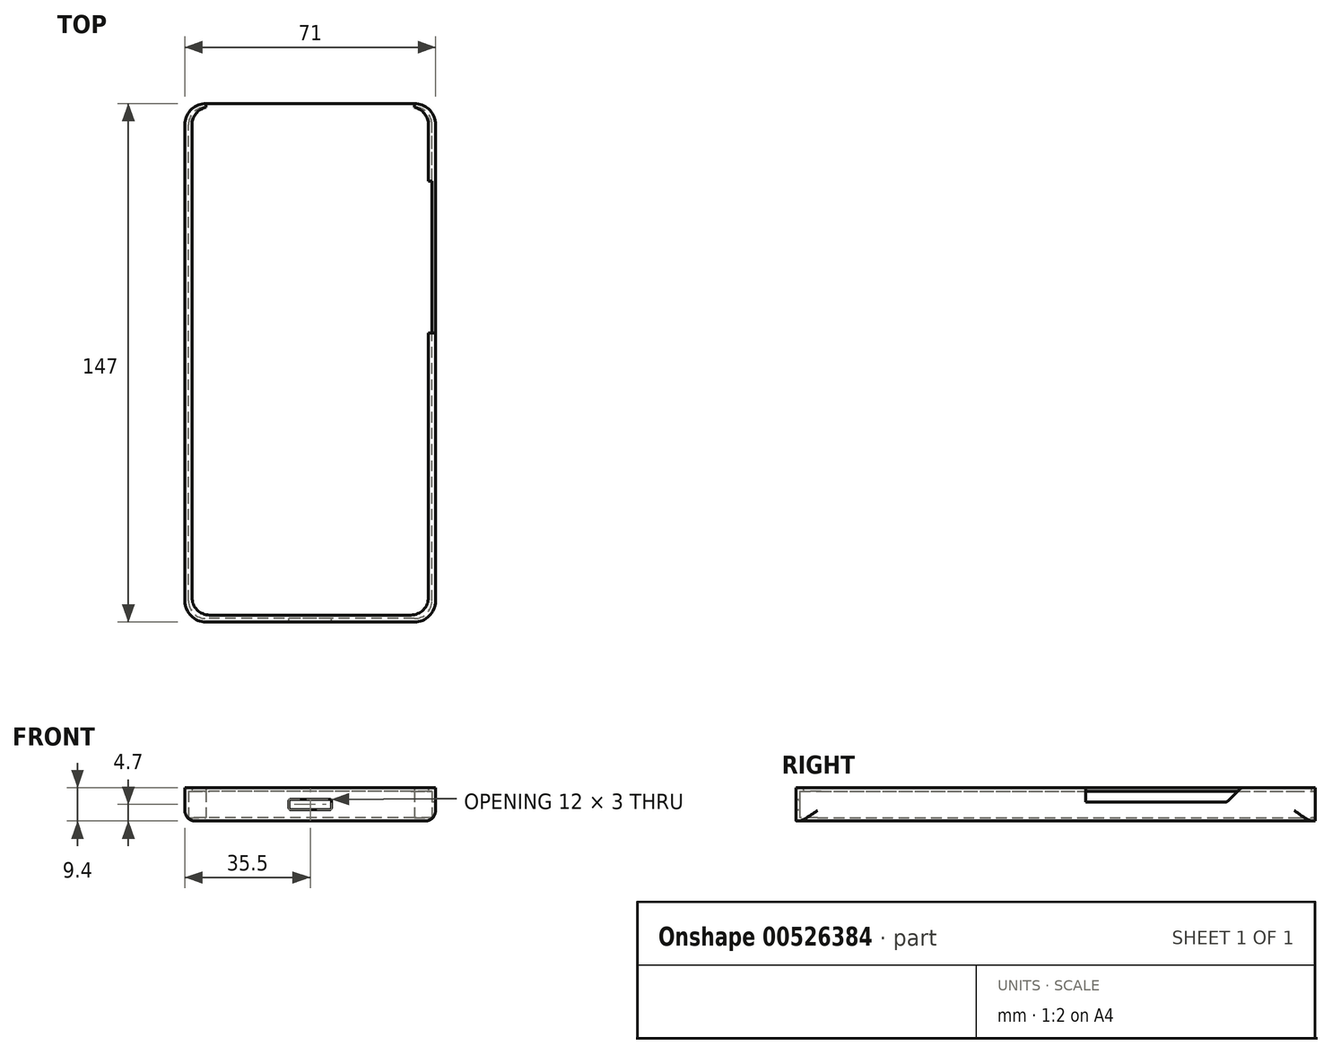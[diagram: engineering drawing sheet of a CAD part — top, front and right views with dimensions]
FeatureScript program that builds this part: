
annotation { "Feature Type Name" : "Feature", "Feature Type Description" : "" }
export const myFeature = defineFeature(function(context is Context, id is Id, definition is map)
    precondition{}
    {
        {
            var Q0;
            Q0=qCreatedBy(makeId("Top.planeOp"),FACE);
            var sketch = newSketch(context, id + "F0", { "sketchPlane" : qUnion([Q0])});
            skLineSegment(sketch, "E0.bottom", {"start": v(29.5, -72.5) * mm, "end": v(-29.5, -72.5) * mm});
            skLineSegment(sketch, "E0.top", {"start": v(29.5, 72.5) * mm, "end": v(-29.5, 72.5) * mm});
            skLineSegment(sketch, "E0.left", {"start": v(34.5, -67.5) * mm, "end": v(34.5, 67.5) * mm});
            skLineSegment(sketch, "E0.right", {"start": v(-34.5, -67.5) * mm, "end": v(-34.5, 67.5) * mm});
            skPoint(sketch, "E0.middle", {"position": v(0, 0) * mm});
            skLineSegment(sketch, "E1.bottom", {"start": v(29.5, -73.5) * mm, "end": v(-29.5, -73.5) * mm});
            skLineSegment(sketch, "E1.top", {"start": v(29.5, 73.5) * mm, "end": v(-29.5, 73.5) * mm});
            skLineSegment(sketch, "E1.left", {"start": v(35.5, -67.5) * mm, "end": v(35.5, 67.5) * mm});
            skLineSegment(sketch, "E1.right", {"start": v(-35.5, -67.5) * mm, "end": v(-35.5, 67.5) * mm});
            skPoint(sketch, "E2.visualSharp", {"position": v(-34.5, 72.5) * mm});
            skArc(sketch, "E2.filletArc", {"start": v(-29.5, 72.5) * mm, "mid": v(-33.04, 71.04) * mm, "end": v(-34.5, 67.5) * mm});
            skPoint(sketch, "E3.visualSharp", {"position": v(-34.5, -72.5) * mm});
            skArc(sketch, "E3.filletArc", {"start": v(-34.5, -67.5) * mm, "mid": v(-33.04, -71.04) * mm, "end": v(-29.5, -72.5) * mm});
            skPoint(sketch, "E4.visualSharp", {"position": v(34.5, -72.5) * mm});
            skArc(sketch, "E4.filletArc", {"start": v(29.5, -72.5) * mm, "mid": v(33.04, -71.04) * mm, "end": v(34.5, -67.5) * mm});
            skPoint(sketch, "E5.visualSharp", {"position": v(34.5, 72.5) * mm});
            skArc(sketch, "E5.filletArc", {"start": v(34.5, 67.5) * mm, "mid": v(33.04, 71.04) * mm, "end": v(29.5, 72.5) * mm});
            skPoint(sketch, "E6.visualSharp", {"position": v(-35.5, 73.5) * mm});
            skArc(sketch, "E6.filletArc", {"start": v(-29.5, 73.5) * mm, "mid": v(-33.74, 71.74) * mm, "end": v(-35.5, 67.5) * mm});
            skPoint(sketch, "E7.visualSharp", {"position": v(-35.5, -73.5) * mm});
            skArc(sketch, "E7.filletArc", {"start": v(-35.5, -67.5) * mm, "mid": v(-33.74, -71.74) * mm, "end": v(-29.5, -73.5) * mm});
            skPoint(sketch, "E8.visualSharp", {"position": v(35.5, -73.5) * mm});
            skArc(sketch, "E8.filletArc", {"start": v(29.5, -73.5) * mm, "mid": v(33.74, -71.74) * mm, "end": v(35.5, -67.5) * mm});
            skPoint(sketch, "E9.visualSharp", {"position": v(35.5, 73.5) * mm});
            skArc(sketch, "E9.filletArc", {"start": v(35.5, 67.5) * mm, "mid": v(33.74, 71.74) * mm, "end": v(29.5, 73.5) * mm});
            skSolve(sketch);
        }
        {
            var Q0;
            Q0=makeQuery(id+"F0.imprint","IMPRINT",FACE,{"disambiguationData":[TD([[makeQuery(id+"F0.imprint","IMPRINT",EDGE,{"derivedFrom":sQuery(id+"F0.wireOp",EDGE,"E0.bottom")}),-1.0]])]});
            extrude(context, id + "F1", {"entities" : qUnion([Q0]), "depth" : 1 * mm});
        }
        {
            var Q0;
            Q0=makeQuery(id+"F0.imprint","IMPRINT",FACE,{"disambiguationData":[TD([[makeQuery(id+"F0.imprint","IMPRINT",EDGE,{"derivedFrom":sQuery(id+"F0.wireOp",EDGE,"E0.bottom")}),1.0]])]});
            extrude(context, id + "F2", {"entities" : qUnion([Q0]), "operationType" : NewBodyOperationType.ADD, "depth" : (1 + 7.4) * mm});
        }
        {
            var Q0;
            Q0=makeQuery(id+"F2.opExtrude","CAP_FACE",FACE,{"disambiguationData":[OSD([sQuery(id+"F0.wireOp",EDGE,"E0.bottom"),sQuery(id+"F0.wireOp",EDGE,"E0.top"),sQuery(id+"F0.wireOp",EDGE,"E0.left"),sQuery(id+"F0.wireOp",EDGE,"E0.right"),sQuery(id+"F0.wireOp",EDGE,"E1.bottom"),sQuery(id+"F0.wireOp",EDGE,"E1.top"),sQuery(id+"F0.wireOp",EDGE,"E1.left"),sQuery(id+"F0.wireOp",EDGE,"E1.right"),sQuery(id+"F0.wireOp",EDGE,"E2.filletArc"),sQuery(id+"F0.wireOp",EDGE,"E3.filletArc"),sQuery(id+"F0.wireOp",EDGE,"E4.filletArc"),sQuery(id+"F0.wireOp",EDGE,"E5.filletArc"),sQuery(id+"F0.wireOp",EDGE,"E6.filletArc"),sQuery(id+"F0.wireOp",EDGE,"E7.filletArc"),sQuery(id+"F0.wireOp",EDGE,"E8.filletArc"),sQuery(id+"F0.wireOp",EDGE,"E9.filletArc")])],"isStart":false});
            var sketch = newSketch(context, id + "F3", { "sketchPlane" : qUnion([Q0])});
            skLineSegment(sketch, "E10.bottom", {"start": v(28.5, -71.5) * mm, "end": v(-28.5, -71.5) * mm});
            skLineSegment(sketch, "E10.top", {"start": v(28.5, 72.5) * mm, "end": v(-28.5, 72.5) * mm});
            skLineSegment(sketch, "E10.left", {"start": v(33.5, -66.5) * mm, "end": v(33.5, 67.5) * mm});
            skLineSegment(sketch, "E10.right", {"start": v(-33.5, -66.5) * mm, "end": v(-33.5, 67.5) * mm});
            skPoint(sketch, "E10.middle", {"position": v(0, 0.5) * mm});
            skPoint(sketch, "E11.visualSharp", {"position": v(-33.5, -71.5) * mm});
            skArc(sketch, "E11.filletArc", {"start": v(-33.5, -66.5) * mm, "mid": v(-32.04, -70.04) * mm, "end": v(-28.5, -71.5) * mm});
            skPoint(sketch, "E12.visualSharp", {"position": v(33.5, -71.5) * mm});
            skArc(sketch, "E12.filletArc", {"start": v(28.5, -71.5) * mm, "mid": v(32.04, -70.04) * mm, "end": v(33.5, -66.5) * mm});
            skPoint(sketch, "E13.visualSharp", {"position": v(33.5, 72.5) * mm});
            skArc(sketch, "E13.filletArc", {"start": v(33.5, 67.5) * mm, "mid": v(32.04, 71.04) * mm, "end": v(28.5, 72.5) * mm});
            skPoint(sketch, "E14.visualSharp", {"position": v(-33.5, 72.5) * mm});
            skArc(sketch, "E14.filletArc", {"start": v(-28.5, 72.5) * mm, "mid": v(-32.04, 71.04) * mm, "end": v(-33.5, 67.5) * mm});
            skSolve(sketch);
        }
        {
            var Q0;
            Q0=makeQuery(id+"F3.imprint","IMPRINT",FACE,{"disambiguationData":[TD([[makeQuery(id+"F3.imprint","IMPRINT",EDGE,{"derivedFrom":sQuery(id+"F3.wireOp",EDGE,"E10.bottom")}),1.0]])]});
            var Q1;
            Q1=makeQuery(id+"F3.imprint","IMPRINT",FACE,{"disambiguationData":[TD([[makeQuery(id+"F3.imprint","IMPRINT",EDGE,{"derivedFrom":makeQuery(id+"F2.opExtrude","CAP_EDGE",EDGE,{"disambiguationData":[OSD([sQuery(id+"F0.wireOp",EDGE,"E0.bottom")])],"isStart":false})}),1.0]])]});
            extrude(context, id + "F4", {"entities" : qUnion([Q0, Q1]), "operationType" : NewBodyOperationType.ADD, "depth" : 1 * mm});
        }
        {
            var Q0;
            Q0=makeQuery(id+"F1.opExtrude","CAP_EDGE",EDGE,{"disambiguationData":[OSD([sQuery(id+"F0.wireOp",EDGE,"E0.right")])],"isStart":false});
            var Q1;
            Q1=makeQuery(id+"F1.opExtrude","CAP_EDGE",EDGE,{"disambiguationData":[OSD([sQuery(id+"F0.wireOp",EDGE,"E0.left")])],"isStart":false});
            var Q2;
            Q2=makeQuery(id+"F2.opExtrude","CAP_EDGE",EDGE,{"disambiguationData":[OSD([sQuery(id+"F0.wireOp",EDGE,"E1.left")])],"isStart":true});
            var Q3;
            Q3=makeQuery(id+"F2.opExtrude","CAP_EDGE",EDGE,{"disambiguationData":[OSD([sQuery(id+"F0.wireOp",EDGE,"E1.right")])],"isStart":true});
            fillet(context, id + "F5", {"entities" : qUnion([Q0, Q1, Q2, Q3]), "radius" : 3 * mm, "allowEdgeOverflow" : false});
        }
        {
            var Q0;
            Q0=makeQuery(id+"F4.boolean.opBoolean","MERGE",FACE,{"derivedFrom":[makeQuery(id+"F2.opExtrude","SWEPT_FACE",FACE,{"disambiguationData":[OSD([sQuery(id+"F0.wireOp",EDGE,"E0.top")])]}),makeQuery(id+"F4.opExtrude","SWEPT_FACE",FACE,{"disambiguationData":[OSD([sQuery(id+"F3.wireOp",EDGE,"E10.top")])]})]});
            extrude(context, id + "F6", {"entities" : qUnion([Q0]), "operationType" : NewBodyOperationType.REMOVE, "endBound" : BoundingType.THROUGH_ALL, "oppositeDirection" : true, "depth" : 25 * mm});
        }
        {
            var Q0;
            {var subQ2=sQuery(id+"F0.wireOp",EDGE,"E0.top");var subQ3=sQuery(id+"F3.wireOp",EDGE,"E14.filletArc");var subQ9=sQuery(id+"F3.wireOp",EDGE,"E10.top");var subQ16=sQuery(id+"F0.wireOp",EDGE,"E1.top");Q0=makeQuery(id+"F6.boolean.opBoolean","SPLIT",FACE,{"disambiguationData":[TD([makeQuery(id+"F6.opExtrude","SWEPT_FACE",FACE,{"disambiguationData":[OSD([subQ2,subQ9,subQ3])]})])],"derivedFrom":makeQuery(id+"F4.boolean.opBoolean","MERGE",FACE,{"derivedFrom":[makeQuery(id+"F2.opExtrude","SWEPT_FACE",FACE,{"disambiguationData":[OSD([subQ16])]}),makeQuery(id+"F4.opExtrude","SWEPT_FACE",FACE,{"disambiguationData":[OSD([subQ16])]})]})});}
            var Q1;
            {var subQ2=sQuery(id+"F3.wireOp",EDGE,"E13.filletArc");var subQ7=sQuery(id+"F3.wireOp",EDGE,"E10.top");var subQ14=sQuery(id+"F0.wireOp",EDGE,"E1.top");var subQ17=sQuery(id+"F0.wireOp",EDGE,"E0.top");Q1=makeQuery(id+"F6.boolean.opBoolean","SPLIT",FACE,{"disambiguationData":[TD([makeQuery(id+"F6.opExtrude","SWEPT_FACE",FACE,{"disambiguationData":[OSD([subQ17,subQ7,subQ2])]})])],"derivedFrom":makeQuery(id+"F4.boolean.opBoolean","MERGE",FACE,{"derivedFrom":[makeQuery(id+"F2.opExtrude","SWEPT_FACE",FACE,{"disambiguationData":[OSD([subQ14])]}),makeQuery(id+"F4.opExtrude","SWEPT_FACE",FACE,{"disambiguationData":[OSD([subQ14])]})]})});}
            extrude(context, id + "F7", {"entities" : qUnion([Q0, Q1]), "operationType" : NewBodyOperationType.REMOVE, "endBound" : BoundingType.UP_TO_NEXT, "oppositeDirection" : true, "depth" : 25 * mm});
        }
        {
            var Q0;
            {var subQ0=sQuery(id+"F0.wireOp",EDGE,"E9.filletArc");var subQ1=sQuery(id+"F0.wireOp",EDGE,"E1.top");var subQ2=makeQuery(id+"F2.opExtrude","SWEPT_FACE",FACE,{"disambiguationData":[OSD([subQ0])]});var subQ3=makeQuery(id+"F4.opExtrude","SWEPT_FACE",FACE,{"disambiguationData":[OSD([subQ0])]});var subQ4=sQuery(id+"F0.wireOp",EDGE,"E5.filletArc");var subQ5=sQuery(id+"F0.wireOp",EDGE,"E0.top");var subQ6=makeQuery(id+"F6.opExtrude","SWEPT_FACE",FACE,{"disambiguationData":[OSD([subQ5,subQ4])]});var subQ7=makeQuery(id+"F4.boolean.opBoolean","MERGE",EDGE,{"derivedFrom":[makeQuery(id+"F2.opExtrude","SWEPT_EDGE",EDGE,{"disambiguationData":[OSD([subQ1,subQ0])]}),makeQuery(id+"F4.opExtrude","SWEPT_EDGE",EDGE,{"disambiguationData":[OSD([subQ1,subQ0])]})]});var subQ22=makeQuery(id+"F2.opExtrude","SWEPT_FACE",FACE,{"disambiguationData":[OSD([subQ1])]});var subQ24=makeQuery(id+"F4.opExtrude","SWEPT_FACE",FACE,{"disambiguationData":[OSD([subQ1])]});var subQ27=makeQuery(id+"F2.opExtrude","CAP_EDGE",EDGE,{"disambiguationData":[OSD([subQ5])],"isStart":false});Q0=makeQuery(id+"F7.boolean.opBoolean","MERGE",EDGE,{"derivedFrom":[makeQuery(id+"F6.boolean.opBoolean","SPLIT",EDGE,{"disambiguationData":[topologyDisambiguationEdgeConnected([subQ22,subQ2,subQ24,subQ3]),TD([makeQuery(id+"F6.opExtrude","SWEPT_FACE",FACE,{"disambiguationData":[OSD([subQ5]),TDD([makeQuery(id+"F4.boolean.opBoolean","SPLIT",EDGE,{"disambiguationData":[TD([makeQuery(id+"F2.opExtrude","SWEPT_FACE",FACE,{"disambiguationData":[OSD([subQ4])]})])],"derivedFrom":subQ27})])]})])],"derivedFrom":subQ7}),makeQuery(id+"F6.boolean.opBoolean","SPLIT",EDGE,{"disambiguationData":[topologyDisambiguationEdgeConnected([subQ2,subQ3,subQ6])],"derivedFrom":subQ7})],"fromTools":[makeQuery(id+"F7.opExtrude","CAP_EDGE",EDGE,{"disambiguationData":[OSD([subQ1,subQ0])],"isStart":true})]});}
            var Q1;
            {var subQ0=sQuery(id+"F0.wireOp",EDGE,"E6.filletArc");var subQ1=sQuery(id+"F0.wireOp",EDGE,"E1.top");var subQ2=makeQuery(id+"F2.opExtrude","SWEPT_FACE",FACE,{"disambiguationData":[OSD([subQ0])]});var subQ3=sQuery(id+"F0.wireOp",EDGE,"E2.filletArc");var subQ4=sQuery(id+"F0.wireOp",EDGE,"E0.top");var subQ5=makeQuery(id+"F6.opExtrude","SWEPT_FACE",FACE,{"disambiguationData":[OSD([subQ4,subQ3])]});var subQ6=makeQuery(id+"F4.opExtrude","SWEPT_FACE",FACE,{"disambiguationData":[OSD([subQ0])]});var subQ7=makeQuery(id+"F4.boolean.opBoolean","MERGE",EDGE,{"derivedFrom":[makeQuery(id+"F2.opExtrude","SWEPT_EDGE",EDGE,{"disambiguationData":[OSD([subQ1,subQ0])]}),makeQuery(id+"F4.opExtrude","SWEPT_EDGE",EDGE,{"disambiguationData":[OSD([subQ1,subQ0])]})]});var subQ22=makeQuery(id+"F2.opExtrude","SWEPT_FACE",FACE,{"disambiguationData":[OSD([subQ1])]});var subQ24=makeQuery(id+"F4.opExtrude","SWEPT_FACE",FACE,{"disambiguationData":[OSD([subQ1])]});var subQ27=makeQuery(id+"F2.opExtrude","CAP_EDGE",EDGE,{"disambiguationData":[OSD([subQ4])],"isStart":false});Q1=makeQuery(id+"F7.boolean.opBoolean","MERGE",EDGE,{"derivedFrom":[makeQuery(id+"F6.boolean.opBoolean","SPLIT",EDGE,{"disambiguationData":[topologyDisambiguationEdgeConnected([subQ22,subQ2,subQ24,subQ6]),TD([makeQuery(id+"F6.opExtrude","SWEPT_FACE",FACE,{"disambiguationData":[OSD([subQ4]),TDD([makeQuery(id+"F4.boolean.opBoolean","SPLIT",EDGE,{"disambiguationData":[TD([makeQuery(id+"F2.opExtrude","SWEPT_FACE",FACE,{"disambiguationData":[OSD([sQuery(id+"F0.wireOp",EDGE,"E5.filletArc")])]})])],"derivedFrom":subQ27})])]})])],"derivedFrom":subQ7}),makeQuery(id+"F6.boolean.opBoolean","SPLIT",EDGE,{"disambiguationData":[topologyDisambiguationEdgeConnected([subQ2,subQ6,subQ5])],"derivedFrom":subQ7})],"fromTools":[makeQuery(id+"F7.opExtrude","CAP_EDGE",EDGE,{"disambiguationData":[OSD([subQ1,subQ0])],"isStart":true})]});}
            var Q2;
            {var subQ0=sQuery(id+"F0.wireOp",EDGE,"E2.filletArc");var subQ1=sQuery(id+"F0.wireOp",EDGE,"E0.top");Q2=makeQuery(id+"F6.boolean.opBoolean","MERGE",EDGE,{"derivedFrom":[makeQuery(id+"F2.opExtrude","SWEPT_EDGE",EDGE,{"disambiguationData":[OSD([subQ1,subQ0])]}),makeQuery(id+"F6.opExtrude","CAP_EDGE",EDGE,{"disambiguationData":[OSD([subQ1,subQ0])],"isStart":true})]});}
            var Q3;
            {var subQ0=sQuery(id+"F0.wireOp",EDGE,"E5.filletArc");var subQ1=sQuery(id+"F0.wireOp",EDGE,"E0.top");Q3=makeQuery(id+"F6.boolean.opBoolean","MERGE",EDGE,{"derivedFrom":[makeQuery(id+"F2.opExtrude","SWEPT_EDGE",EDGE,{"disambiguationData":[OSD([subQ1,subQ0])]}),makeQuery(id+"F6.opExtrude","CAP_EDGE",EDGE,{"disambiguationData":[OSD([subQ1,subQ0])],"isStart":true})]});}
            fillet(context, id + "F8", {"entities" : qUnion([Q0, Q1, Q2, Q3]), "radius" : 0.5 * mm, "tangentPropagation" : true, "allowEdgeOverflow" : false});
        }
        {
            var Q0;
            Q0=makeQuery(id+"F2.opExtrude","SWEPT_FACE",FACE,{"disambiguationData":[OSD([sQuery(id+"F0.wireOp",EDGE,"E0.bottom")])]});
            var sketch = newSketch(context, id + "F9", { "sketchPlane" : qUnion([Q0])});
            skLineSegment(sketch, "E15", {"start": v(0, 1) * mm, "end": v(0, 8.4) * mm, "construction": true});
            skLineSegment(sketch, "E16.bottom", {"start": v(-6, 6.2) * mm, "end": v(6, 6.2) * mm});
            skLineSegment(sketch, "E16.top", {"start": v(-6, 3.2) * mm, "end": v(6, 3.2) * mm});
            skLineSegment(sketch, "E16.left", {"start": v(-6, 6.2) * mm, "end": v(-6, 3.2) * mm});
            skLineSegment(sketch, "E16.right", {"start": v(6, 6.2) * mm, "end": v(6, 3.2) * mm});
            skPoint(sketch, "E16.middle", {"position": v(0, 4.7) * mm});
            skSolve(sketch);
        }
        {
            var Q0;
            Q0=makeQuery(id+"F9.imprint","IMPRINT",FACE,{"disambiguationData":[TD([[makeQuery(id+"F9.imprint","IMPRINT",EDGE,{"derivedFrom":sQuery(id+"F9.wireOp",EDGE,"E16.bottom")}),-1.0]])]});
            extrude(context, id + "F10", {"entities" : qUnion([Q0]), "operationType" : NewBodyOperationType.REMOVE, "endBound" : BoundingType.UP_TO_NEXT, "oppositeDirection" : true, "depth" : 25 * mm});
        }
        {
            var Q0;
            Q0=makeQuery(id+"F10.boolean.opBoolean","COPY",EDGE,{"derivedFrom":makeQuery(id+"F10.opExtrude","SWEPT_EDGE",EDGE,{"disambiguationData":[OSD([sQuery(id+"F9.wireOp",EDGE,"E16.top"),sQuery(id+"F9.wireOp",EDGE,"E16.right")])]})});
            var Q1;
            Q1=makeQuery(id+"F10.boolean.opBoolean","COPY",EDGE,{"derivedFrom":makeQuery(id+"F10.opExtrude","SWEPT_EDGE",EDGE,{"disambiguationData":[OSD([sQuery(id+"F9.wireOp",EDGE,"E16.top"),sQuery(id+"F9.wireOp",EDGE,"E16.left")])]})});
            var Q2;
            Q2=makeQuery(id+"F10.boolean.opBoolean","COPY",EDGE,{"derivedFrom":makeQuery(id+"F10.opExtrude","SWEPT_EDGE",EDGE,{"disambiguationData":[OSD([sQuery(id+"F9.wireOp",EDGE,"E16.bottom"),sQuery(id+"F9.wireOp",EDGE,"E16.right")])]})});
            var Q3;
            Q3=makeQuery(id+"F10.boolean.opBoolean","COPY",EDGE,{"derivedFrom":makeQuery(id+"F10.opExtrude","SWEPT_EDGE",EDGE,{"disambiguationData":[OSD([sQuery(id+"F9.wireOp",EDGE,"E16.bottom"),sQuery(id+"F9.wireOp",EDGE,"E16.left")])]})});
            fillet(context, id + "F11", {"entities" : qUnion([Q0, Q1, Q2, Q3]), "radius" : 0.5 * mm, "tangentPropagation" : true, "allowEdgeOverflow" : false});
        }
        {
            var Q0;
            {var subQ0=sQuery(id+"F0.wireOp",EDGE,"E1.left");Q0=makeQuery(id+"F4.boolean.opBoolean","MERGE",FACE,{"derivedFrom":[makeQuery(id+"F2.opExtrude","SWEPT_FACE",FACE,{"disambiguationData":[OSD([subQ0])]}),makeQuery(id+"F4.opExtrude","SWEPT_FACE",FACE,{"disambiguationData":[OSD([subQ0])]})]});}
            var sketch = newSketch(context, id + "F12", { "sketchPlane" : qUnion([Q0])});
            skLineSegment(sketch, "E17.bottom", {"start": v(48.48, 9.4) * mm, "end": v(8.48, 9.4) * mm});
            skLineSegment(sketch, "E17.top", {"start": v(48.48, 5.4) * mm, "end": v(8.48, 5.4) * mm});
            skLineSegment(sketch, "E17.left", {"start": v(48.48, 9.4) * mm, "end": v(48.48, 5.4) * mm});
            skLineSegment(sketch, "E17.right", {"start": v(8.48, 9.4) * mm, "end": v(8.48, 5.4) * mm});
            skSolve(sketch);
        }
        {
            var Q0;
            Q0=qSketchRegion(id+"F12",true);
            extrude(context, id + "F13", {"entities" : qUnion([Q0]), "operationType" : NewBodyOperationType.REMOVE, "endBound" : BoundingType.UP_TO_NEXT, "oppositeDirection" : true, "depth" : 25 * mm});
        }
        {
            var Q0;
            Q0=makeQuery(id+"F13.boolean.opBoolean","COPY",EDGE,{"derivedFrom":makeQuery(id+"F13.opExtrude","SWEPT_EDGE",EDGE,{"disambiguationData":[OSD([sQuery(id+"F0.wireOp",EDGE,"E1.left"),sQuery(id+"F12.wireOp",EDGE,"E17.bottom"),sQuery(id+"F12.wireOp",EDGE,"E17.left")])]})});
            var Q1;
            Q1=makeQuery(id+"F13.boolean.opBoolean","COPY",EDGE,{"derivedFrom":makeQuery(id+"F13.opExtrude","SWEPT_EDGE",EDGE,{"disambiguationData":[OSD([sQuery(id+"F0.wireOp",EDGE,"E1.left"),sQuery(id+"F12.wireOp",EDGE,"E17.bottom"),sQuery(id+"F12.wireOp",EDGE,"E17.right")])]})});
            chamfer(context, id + "F14", {"entities" : qUnion([Q0, Q1]), "width" : 4 * mm, "tangentPropagation" : true});
        }
        {
            var Q0;
            Q0=makeQuery(id+"F14.opChamfer","BLEND_EDGE",EDGE,{"blendedFrom":[makeQuery(id+"F13.boolean.opBoolean","COPY",EDGE,{"derivedFrom":makeQuery(id+"F13.opExtrude","SWEPT_EDGE",EDGE,{"disambiguationData":[OSD([sQuery(id+"F0.wireOp",EDGE,"E1.left"),sQuery(id+"F12.wireOp",EDGE,"E17.bottom"),sQuery(id+"F12.wireOp",EDGE,"E17.left")])]})}),makeQuery(id+"F13.boolean.opBoolean","COPY",FACE,{"derivedFrom":makeQuery(id+"F13.opExtrude","SWEPT_FACE",FACE,{"disambiguationData":[OSD([sQuery(id+"F12.wireOp",EDGE,"E17.top")])]})})],"blendedInto":[makeQuery(id+"F13.boolean.opBoolean","COPY",FACE,{"derivedFrom":makeQuery(id+"F13.opExtrude","SWEPT_FACE",FACE,{"disambiguationData":[OSD([sQuery(id+"F12.wireOp",EDGE,"E17.top")])]})})]});
            var Q1;
            Q1=makeQuery(id+"F14.opChamfer","BLEND_EDGE",EDGE,{"blendedFrom":[makeQuery(id+"F13.boolean.opBoolean","COPY",EDGE,{"derivedFrom":makeQuery(id+"F13.opExtrude","SWEPT_EDGE",EDGE,{"disambiguationData":[OSD([sQuery(id+"F0.wireOp",EDGE,"E1.left"),sQuery(id+"F12.wireOp",EDGE,"E17.bottom"),sQuery(id+"F12.wireOp",EDGE,"E17.right")])]})}),makeQuery(id+"F13.boolean.opBoolean","COPY",FACE,{"derivedFrom":makeQuery(id+"F13.opExtrude","SWEPT_FACE",FACE,{"disambiguationData":[OSD([sQuery(id+"F12.wireOp",EDGE,"E17.top")])]})})],"blendedInto":[makeQuery(id+"F13.boolean.opBoolean","COPY",FACE,{"derivedFrom":makeQuery(id+"F13.opExtrude","SWEPT_FACE",FACE,{"disambiguationData":[OSD([sQuery(id+"F12.wireOp",EDGE,"E17.top")])]})})]});
            fillet(context, id + "F15", {"entities" : qUnion([Q0, Q1]), "radius" : 1 * mm, "tangentPropagation" : true, "allowEdgeOverflow" : false});
        }
        {
            var Q0;
            {var subQ0=sQuery(id+"F3.wireOp",EDGE,"E13.filletArc");var subQ1=sQuery(id+"F12.wireOp",EDGE,"E17.left");var subQ2=sQuery(id+"F0.wireOp",EDGE,"E9.filletArc");var subQ3=sQuery(id+"F0.wireOp",EDGE,"E1.left");var subQ4=sQuery(id+"F3.wireOp",EDGE,"E10.left");Q0=makeQuery(id+"F14.opChamfer","BLEND_EDGE",EDGE,{"blendedFrom":[makeQuery(id+"F13.boolean.opBoolean","COPY",EDGE,{"derivedFrom":makeQuery(id+"F13.opExtrude","SWEPT_EDGE",EDGE,{"disambiguationData":[OSD([subQ3,sQuery(id+"F12.wireOp",EDGE,"E17.bottom"),subQ1])]})}),makeQuery(id+"F13.boolean.opBoolean","SPLIT",FACE,{"disambiguationData":[TD([makeQuery(id+"F2.opExtrude","SWEPT_FACE",FACE,{"disambiguationData":[OSD([subQ2])]})])],"derivedFrom":makeQuery(id+"F4.opExtrude","CAP_FACE",FACE,{"disambiguationData":[OSD([sQuery(id+"F0.wireOp",EDGE,"E1.bottom"),sQuery(id+"F0.wireOp",EDGE,"E1.top"),subQ3,sQuery(id+"F0.wireOp",EDGE,"E1.right"),sQuery(id+"F0.wireOp",EDGE,"E6.filletArc"),sQuery(id+"F0.wireOp",EDGE,"E7.filletArc"),sQuery(id+"F0.wireOp",EDGE,"E8.filletArc"),subQ2,sQuery(id+"F3.wireOp",EDGE,"E10.bottom"),sQuery(id+"F3.wireOp",EDGE,"E10.top"),subQ4,sQuery(id+"F3.wireOp",EDGE,"E10.right"),sQuery(id+"F3.wireOp",EDGE,"E11.filletArc"),sQuery(id+"F3.wireOp",EDGE,"E12.filletArc"),subQ0,sQuery(id+"F3.wireOp",EDGE,"E14.filletArc")])],"isStart":false})})],"blendedInto":[makeQuery(id+"F13.boolean.opBoolean","SPLIT",FACE,{"disambiguationData":[TD([makeQuery(id+"F2.opExtrude","SWEPT_FACE",FACE,{"disambiguationData":[OSD([subQ2])]})])],"derivedFrom":makeQuery(id+"F4.opExtrude","CAP_FACE",FACE,{"disambiguationData":[OSD([sQuery(id+"F0.wireOp",EDGE,"E1.bottom"),sQuery(id+"F0.wireOp",EDGE,"E1.top"),subQ3,sQuery(id+"F0.wireOp",EDGE,"E1.right"),sQuery(id+"F0.wireOp",EDGE,"E6.filletArc"),sQuery(id+"F0.wireOp",EDGE,"E7.filletArc"),sQuery(id+"F0.wireOp",EDGE,"E8.filletArc"),subQ2,sQuery(id+"F3.wireOp",EDGE,"E10.bottom"),sQuery(id+"F3.wireOp",EDGE,"E10.top"),subQ4,sQuery(id+"F3.wireOp",EDGE,"E10.right"),sQuery(id+"F3.wireOp",EDGE,"E11.filletArc"),sQuery(id+"F3.wireOp",EDGE,"E12.filletArc"),subQ0,sQuery(id+"F3.wireOp",EDGE,"E14.filletArc")])],"isStart":false})})]});}
            var Q1;
            {var subQ0=sQuery(id+"F3.wireOp",EDGE,"E11.filletArc");var subQ1=sQuery(id+"F3.wireOp",EDGE,"E10.right");var subQ2=sQuery(id+"F3.wireOp",EDGE,"E10.bottom");var subQ3=sQuery(id+"F0.wireOp",EDGE,"E8.filletArc");var subQ4=sQuery(id+"F0.wireOp",EDGE,"E7.filletArc");var subQ5=sQuery(id+"F0.wireOp",EDGE,"E1.bottom");var subQ8=sQuery(id+"F0.wireOp",EDGE,"E1.left");var subQ9=sQuery(id+"F3.wireOp",EDGE,"E10.left");var subQ10=sQuery(id+"F0.wireOp",EDGE,"E1.right");var subQ11=sQuery(id+"F0.wireOp",EDGE,"E6.filletArc");var subQ12=sQuery(id+"F12.wireOp",EDGE,"E17.right");var subQ13=sQuery(id+"F3.wireOp",EDGE,"E12.filletArc");var subQ14=sQuery(id+"F3.wireOp",EDGE,"E14.filletArc");Q1=makeQuery(id+"F14.opChamfer","BLEND_EDGE",EDGE,{"blendedFrom":[makeQuery(id+"F13.boolean.opBoolean","COPY",EDGE,{"derivedFrom":makeQuery(id+"F13.opExtrude","SWEPT_EDGE",EDGE,{"disambiguationData":[OSD([subQ8,sQuery(id+"F12.wireOp",EDGE,"E17.bottom"),subQ12])]})}),makeQuery(id+"F13.boolean.opBoolean","SPLIT",FACE,{"disambiguationData":[TD([makeQuery(id+"F2.opExtrude","SWEPT_FACE",FACE,{"disambiguationData":[OSD([subQ5])]})])],"derivedFrom":makeQuery(id+"F4.opExtrude","CAP_FACE",FACE,{"disambiguationData":[OSD([subQ5,sQuery(id+"F0.wireOp",EDGE,"E1.top"),subQ8,subQ10,subQ11,subQ4,subQ3,sQuery(id+"F0.wireOp",EDGE,"E9.filletArc"),subQ2,sQuery(id+"F3.wireOp",EDGE,"E10.top"),subQ9,subQ1,subQ0,subQ13,sQuery(id+"F3.wireOp",EDGE,"E13.filletArc"),subQ14])],"isStart":false})})],"blendedInto":[makeQuery(id+"F13.boolean.opBoolean","SPLIT",FACE,{"disambiguationData":[TD([makeQuery(id+"F2.opExtrude","SWEPT_FACE",FACE,{"disambiguationData":[OSD([subQ5])]})])],"derivedFrom":makeQuery(id+"F4.opExtrude","CAP_FACE",FACE,{"disambiguationData":[OSD([subQ5,sQuery(id+"F0.wireOp",EDGE,"E1.top"),subQ8,subQ10,subQ11,subQ4,subQ3,sQuery(id+"F0.wireOp",EDGE,"E9.filletArc"),subQ2,sQuery(id+"F3.wireOp",EDGE,"E10.top"),subQ9,subQ1,subQ0,subQ13,sQuery(id+"F3.wireOp",EDGE,"E13.filletArc"),subQ14])],"isStart":false})})]});}
            fillet(context, id + "F16", {"entities" : qUnion([Q0, Q1]), "radius" : 1 * mm, "tangentPropagation" : true, "allowEdgeOverflow" : false});
        }
    });
